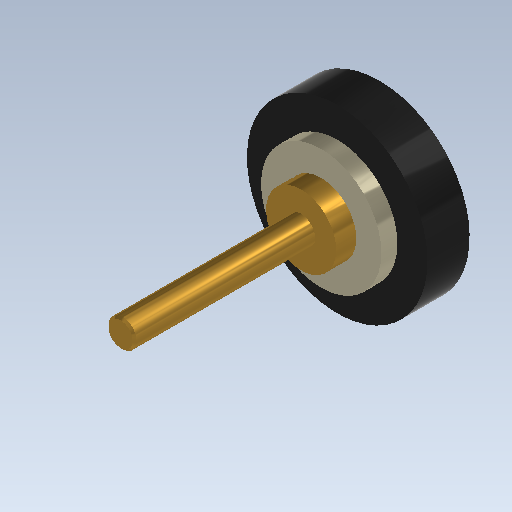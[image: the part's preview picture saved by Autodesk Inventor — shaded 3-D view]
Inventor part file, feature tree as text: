
AUTODESK INVENTOR PART (.ipt)
format: ipt  version: 2020 (Build 240168000, 168)  size: 141,824 bytes
history: native  units: mm
features: other x1, revolve x1, chamfer x1, sketch x1
ambient origin geometry x8: Origin, YZ Plane, XZ Plane, XY Plane, X Axis, Y Axis, Z Axis, Center Point
bodies: Body1 (feature_tree)
feature tree (4):
  other  "Твердое тело1"
  revolve  "Вращение1"
  chamfer  "Фаска1"  Distance=1.4mm
  sketch  "Эскиз1"
